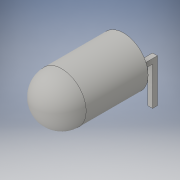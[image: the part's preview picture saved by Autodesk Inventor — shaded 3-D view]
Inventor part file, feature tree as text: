
AUTODESK INVENTOR PART (.ipt)
format: ipt  version: 2016 (Build 200138000, 138)  size: 144,384 bytes
history: native  units: mm
features: sketch x3, extrude x2, other x1, revolve x1
ambient origin geometry x8: Origin, YZ Plane, XZ Plane, XY Plane, X Axis, Y Axis, Z Axis, Center Point
bodies: Body1 (feature_tree)
feature tree (7):
  other  "ソリッド1"
  revolve  "回転1"
  extrude  "押し出し1"  Depth=9.0mm
  extrude  "押し出し2"  Depth=5.1mm
  sketch  "スケッチ1"
  sketch  "スケッチ2"
  sketch  "スケッチ3"
